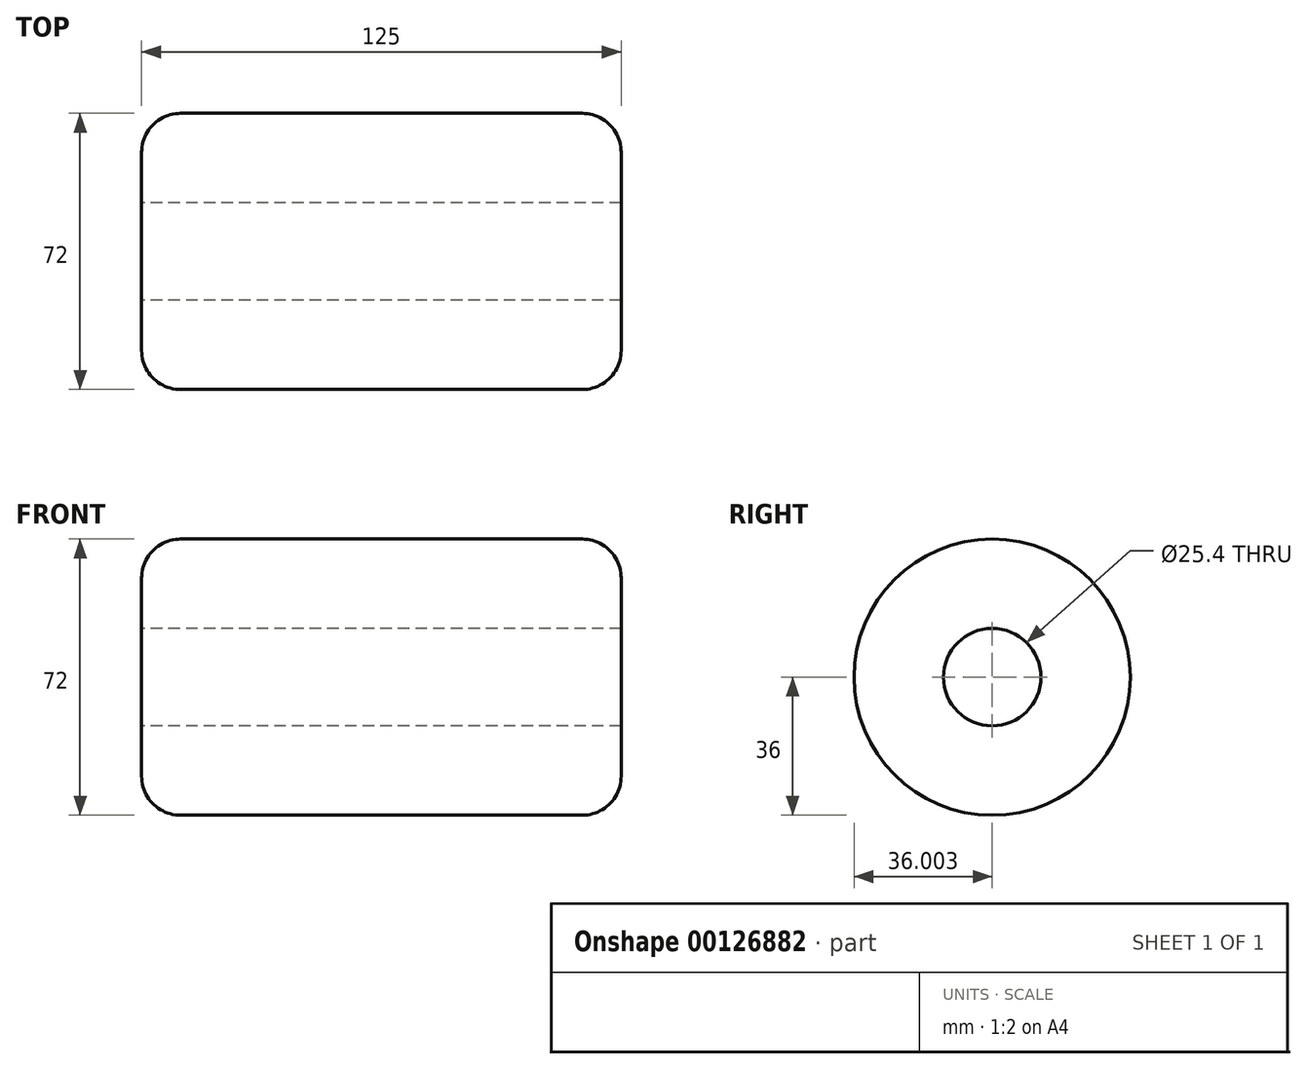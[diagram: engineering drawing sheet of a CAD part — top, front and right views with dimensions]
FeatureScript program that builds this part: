
annotation { "Feature Type Name" : "Feature", "Feature Type Description" : "" }
export const myFeature = defineFeature(function(context is Context, id is Id, definition is map)
    precondition{}
    {
        {
            var Q0;
            Q0=qCreatedBy(makeId("Right.planeOp"),FACE);
            var sketch = newSketch(context, id + "F0", { "sketchPlane" : qUnion([Q0])});
            skCircle(sketch, "E0", {"center": v(-19.98, 22.5) * mm, "radius": 36 * mm});
            skSolve(sketch);
        }
        {
            var Q0;
            Q0=makeQuery(id+"F0.imprint","IMPRINT",FACE,{"disambiguationData":[TD([[makeQuery(id+"F0.imprint","IMPRINT",EDGE,{"derivedFrom":sQuery(id+"F0.wireOp",EDGE,"E0")}),1.0]])]});
            extrude(context, id + "F1", {"entities" : qUnion([Q0]), "depth" : 125 * mm});
        }
        {
            var Q0;
            Q0=makeQuery(id+"F1.opExtrude","CAP_FACE",FACE,{"disambiguationData":[OSD([sQuery(id+"F0.wireOp",EDGE,"E0")])],"isStart":true});
            var sketch = newSketch(context, id + "F2", { "sketchPlane" : qUnion([Q0])});
            skPoint(sketch, "E1", {"position": v(19.98, 22.5) * mm});
            skCircle(sketch, "E2", {"center": v(19.98, 22.5) * mm, "radius": 12.7 * mm});
            skSolve(sketch);
        }
        {
            var Q0;
            Q0=makeQuery(id+"F2.imprint","IMPRINT",FACE,{"disambiguationData":[TD([[makeQuery(id+"F2.imprint","IMPRINT",EDGE,{"derivedFrom":sQuery(id+"F2.wireOp",EDGE,"E2")}),1.0]])]});
            extrude(context, id + "F3", {"entities" : qUnion([Q0]), "operationType" : NewBodyOperationType.REMOVE, "oppositeDirection" : true, "depth" : 254 * mm});
        }
        {
            var Q0;
            Q0=makeQuery(id+"F1.opExtrude","CAP_EDGE",EDGE,{"disambiguationData":[OSD([sQuery(id+"F0.wireOp",EDGE,"E0")])],"isStart":true});
            var Q1;
            Q1=makeQuery(id+"F1.opExtrude","CAP_EDGE",EDGE,{"disambiguationData":[OSD([sQuery(id+"F0.wireOp",EDGE,"E0")])],"isStart":false});
            fillet(context, id + "F4", {"entities" : qUnion([Q0, Q1]), "radius" : 10.16 * mm, "tangentPropagation" : true, "allowEdgeOverflow" : false});
        }
    });
